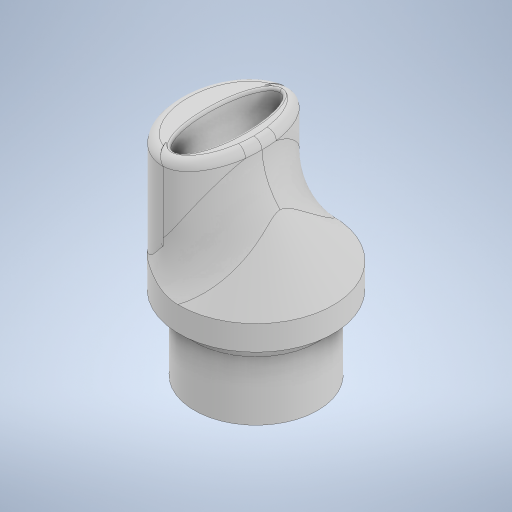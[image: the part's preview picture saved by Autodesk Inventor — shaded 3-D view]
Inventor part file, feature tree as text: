
AUTODESK INVENTOR PART (.ipt)
format: ipt  version: 2024 (Build 280153000, 153)  size: 596,480 bytes
history: native  units: mm
features: extrude x10, sketch x10, fillet x9, other x1, chamfer x1
ambient origin geometry x8: Origin, YZ Plane, XZ Plane, XY Plane, X Axis, Y Axis, Z Axis, Center Point
bodies: Body1 (feature_tree)
feature tree (31):
  other  "Твердое тело1"
  extrude  "Выдавливание1"  Depth=18.7mm
  extrude  "Выдавливание2"  Depth=14.7mm
  extrude  "Выдавливание5"  Depth=15.0mm TaperAngle=0.0deg
  extrude  "Выдавливание6"  Depth=18.0mm TaperAngle=0.0deg
  chamfer  "Фаска2"  Distance=18.0mm
  fillet  "Сопряжение1"  Radius=11.0mm
  extrude  "Выдавливание7"  Depth=8.5mm
  fillet  "Сопряжение2"  Radius=8.0mm
  fillet  "Сопряжение3"  [1 undecoded]
  extrude  "Выдавливание8"  Depth=6.0mm
  extrude  "Выдавливание9"  Depth=8.67mm
  fillet  "Сопряжение4"  Radius=14.0mm
  fillet  "Сопряжение5"  Radius=14.96mm
  extrude  "Выдавливание10"  Depth=12.96mm
  fillet  "Сопряжение6"  Radius=14.0mm
  extrude  "Выдавливание11"  Depth=1.8mm
  fillet  "Сопряжение7"  Radius=0.5mm
  fillet  "Сопряжение8"  Radius=19.0mm
  fillet  "Сопряжение9"  Radius=1.0mm
  extrude  "Выдавливание12"  Depth=3.0mm TaperAngle=0.0deg
  sketch  "Эскиз1"
  sketch  "Эскиз2"
  sketch  "Эскиз5"
  sketch  "Эскиз6"
  sketch  "Эскиз7"
  sketch  "Эскиз8"
  sketch  "Эскиз9"
  sketch  "Эскиз10"
  sketch  "Эскиз11"
  sketch  "Эскиз12"
note: 1 required parameter value undecoded (feature->parameter linkage not recoverable at this tier; creation-order binding heuristic only, values carry confidence <= 0.55)
